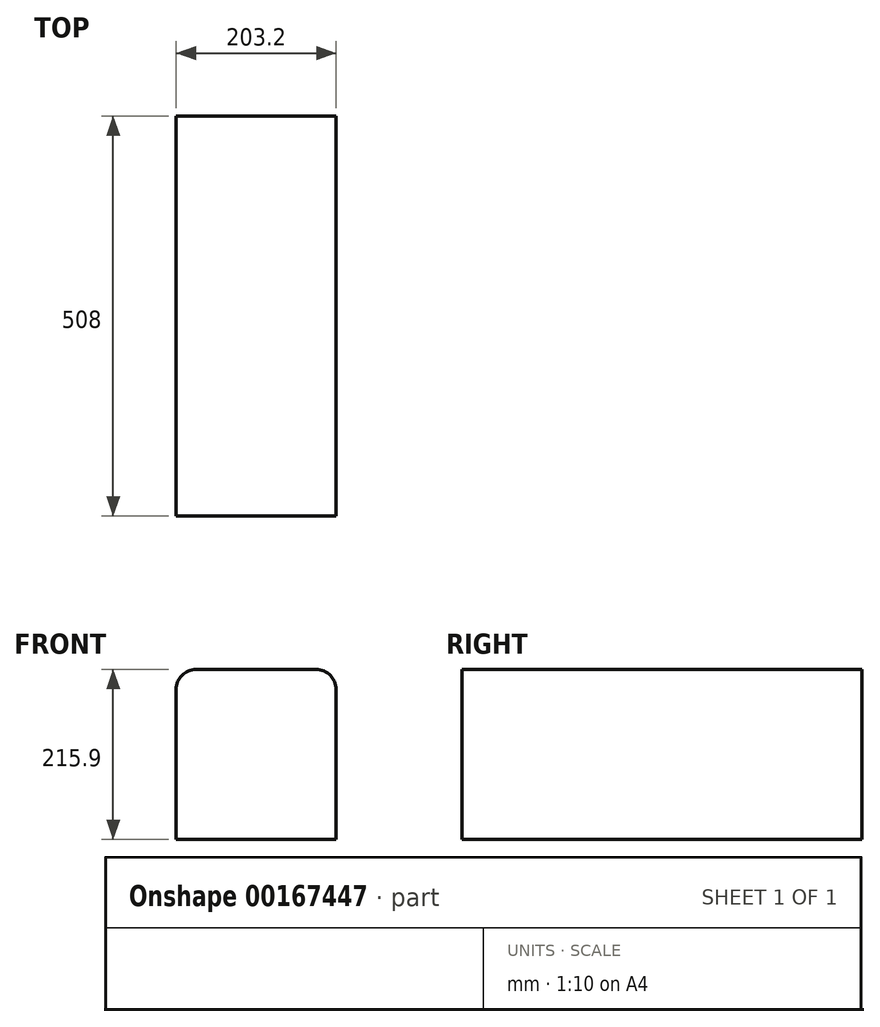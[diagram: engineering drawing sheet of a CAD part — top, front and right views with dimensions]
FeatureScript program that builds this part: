
annotation { "Feature Type Name" : "Feature", "Feature Type Description" : "" }
export const myFeature = defineFeature(function(context is Context, id is Id, definition is map)
    precondition{}
    {
        {
            var Q0;
            Q0=qCreatedBy(makeId("Front.planeOp"),FACE);
            var sketch = newSketch(context, id + "F0", { "sketchPlane" : qUnion([Q0])});
            skLineSegment(sketch, "E0.bottom", {"start": v(-90.79, 215.9) * mm, "end": v(61.61, 215.9) * mm});
            skLineSegment(sketch, "E0.top", {"start": v(-116.19, 0) * mm, "end": v(87.01, 0) * mm});
            skLineSegment(sketch, "E0.left", {"start": v(-116.19, 190.5) * mm, "end": v(-116.19, 0) * mm});
            skLineSegment(sketch, "E0.right", {"start": v(87.01, 190.5) * mm, "end": v(87.01, 0) * mm});
            skPoint(sketch, "E1.visualSharp", {"position": v(-116.19, 215.9) * mm});
            skArc(sketch, "E1.filletArc", {"start": v(-90.79, 215.9) * mm, "mid": v(-108.75, 208.46) * mm, "end": v(-116.19, 190.5) * mm});
            skPoint(sketch, "E2.visualSharp", {"position": v(87.01, 215.9) * mm});
            skArc(sketch, "E2.filletArc", {"start": v(87.01, 190.5) * mm, "mid": v(79.57, 208.46) * mm, "end": v(61.61, 215.9) * mm});
            skSolve(sketch);
        }
        {
            var Q0;
            Q0 = qSketchRegion(id + "F0", true);
            extrude(context, id + "F1", {"entities" : qUnion([Q0]), "depth" : 508 * mm});
        }
    });
